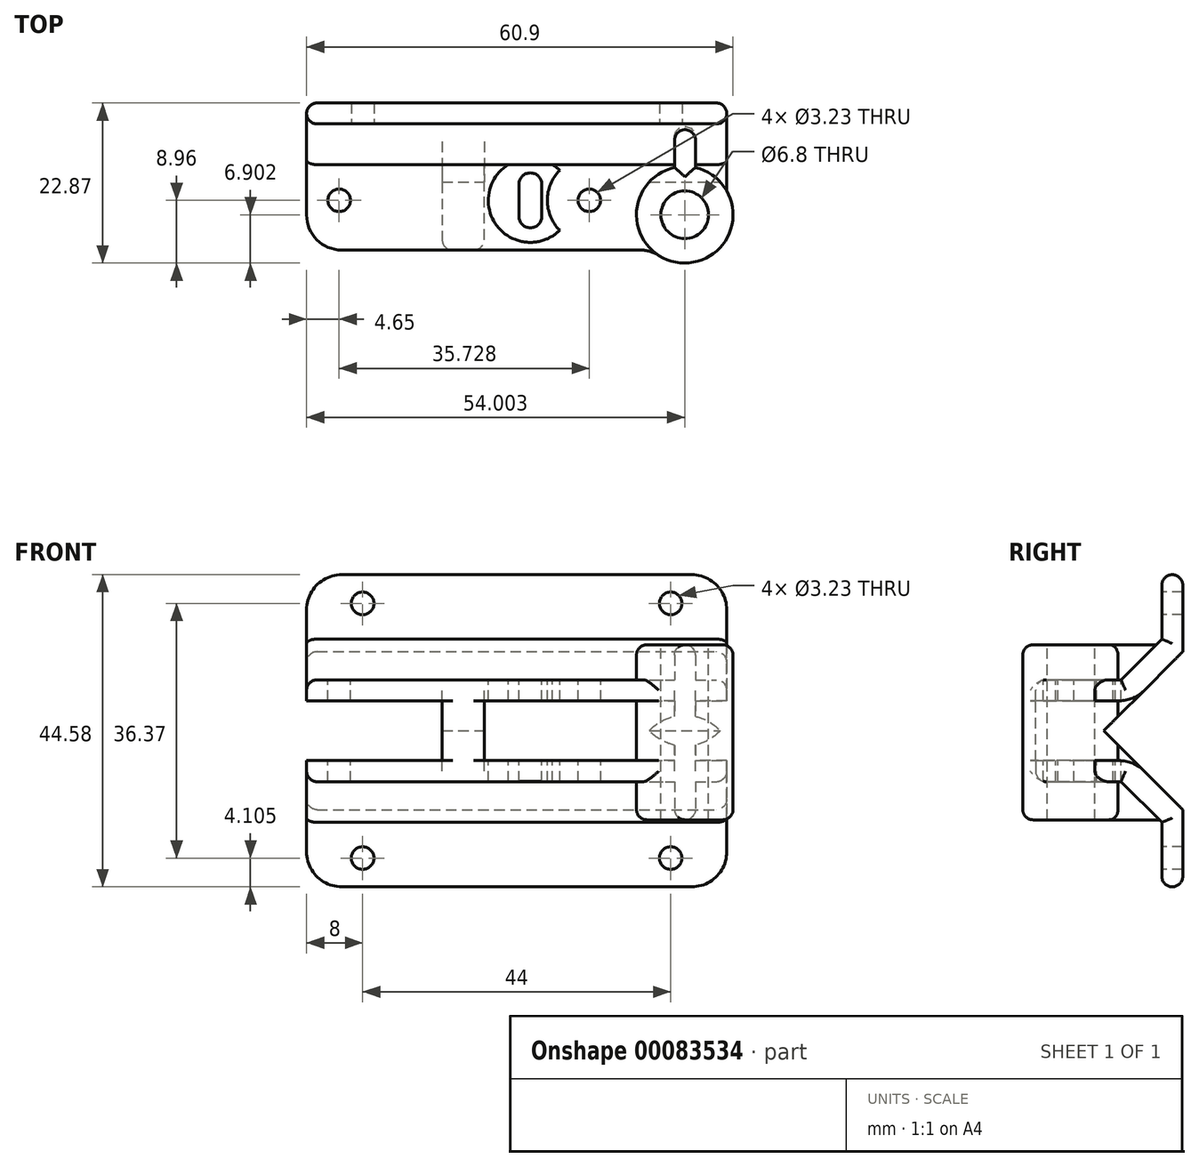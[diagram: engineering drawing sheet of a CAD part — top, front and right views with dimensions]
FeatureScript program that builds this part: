
annotation { "Feature Type Name" : "Feature", "Feature Type Description" : "" }
export const myFeature = defineFeature(function(context is Context, id is Id, definition is map)
    precondition{}
    {
        {
            var Q0;
            Q0=qCreatedBy(makeId("Right.planeOp"),FACE);
            var sketch = newSketch(context, id + "F0", { "sketchPlane" : qUnion([Q0])});
            skLineSegment(sketch, "E0", {"start": v(0, 0) * mm, "end": v(13.44, -13.44) * mm});
            skLineSegment(sketch, "E1", {"start": v(13.44, -13.44) * mm, "end": v(14.47, -12.4) * mm});
            skLineSegment(sketch, "E2", {"start": v(14.47, -12.4) * mm, "end": v(2.06, 0) * mm});
            skLineSegment(sketch, "E3", {"start": v(2.06, 0) * mm, "end": v(14.47, 12.4) * mm});
            skLineSegment(sketch, "E4", {"start": v(14.47, 12.4) * mm, "end": v(13.44, 13.44) * mm});
            skLineSegment(sketch, "E5", {"start": v(13.44, 13.44) * mm, "end": v(0, 0) * mm});
            skLineSegment(sketch, "E6", {"start": v(2.06, 0) * mm, "end": v(29.35, 0) * mm, "construction": true});
            skLineSegment(sketch, "E7.bottom", {"start": v(11.44, 23.19) * mm, "end": v(15.44, 23.19) * mm});
            skLineSegment(sketch, "E7.top", {"start": v(11.44, 13.19) * mm, "end": v(15.44, 13.19) * mm});
            skLineSegment(sketch, "E7.left", {"start": v(11.44, 23.19) * mm, "end": v(11.44, 13.19) * mm});
            skLineSegment(sketch, "E7.right", {"start": v(15.44, 23.19) * mm, "end": v(15.44, 13.19) * mm});
            skLineSegment(sketch, "E8", {"start": v(15.44, 18.19) * mm, "end": v(11.44, 18.19) * mm});
            skLineSegment(sketch, "E9", {"start": v(13.44, 23.19) * mm, "end": v(13.44, 13.19) * mm, "construction": true});
            skLineSegment(sketch, "E10", {"start": v(13.19, 23.19) * mm, "end": v(13.44, 22.94) * mm});
            skLineSegment(sketch, "E11", {"start": v(13.44, 22.94) * mm, "end": v(13.69, 23.19) * mm});
            skLineSegment(sketch, "E12", {"start": v(13.19, 13.19) * mm, "end": v(13.44, 13.44) * mm});
            skLineSegment(sketch, "E13", {"start": v(13.44, 13.44) * mm, "end": v(13.69, 13.19) * mm});
            skLineSegment(sketch, "E14.MirrorCS", {"start": v(12.4, 12.4) * mm, "end": v(13.44, 13.44) * mm});
            skLineSegment(sketch, "E15.MirrorCS", {"start": v(13.69, 23.19) * mm, "end": v(13.44, 22.94) * mm});
            skLineSegment(sketch, "E16.MirrorCS", {"start": v(13.44, 22.94) * mm, "end": v(13.19, 23.19) * mm});
            skLineSegment(sketch, "E17.MirrorCS", {"start": v(13.69, 13.19) * mm, "end": v(13.44, 13.44) * mm});
            skLineSegment(sketch, "E18.MirrorCS", {"start": v(15.44, 23.19) * mm, "end": v(11.44, 23.19) * mm});
            skLineSegment(sketch, "E19.MirrorCS", {"start": v(13.44, 13.44) * mm, "end": v(13.19, 13.19) * mm});
            skLineSegment(sketch, "E20.MirrorCS", {"start": v(11.44, 18.19) * mm, "end": v(15.44, 18.19) * mm});
            skLineSegment(sketch, "E21.MirrorCS", {"start": v(15.44, 13.19) * mm, "end": v(11.44, 13.19) * mm});
            skLineSegment(sketch, "E22", {"start": v(13.44, 13.44) * mm, "end": v(13.44, -13.44) * mm, "construction": true});
            skPoint(sketch, "E23", {"position": v(13.44, 0) * mm});
            skLineSegment(sketch, "E24", {"start": v(11.44, 19.74) * mm, "end": v(15.44, 19.74) * mm});
            skLineSegment(sketch, "E25.MirrorCS", {"start": v(11.44, 16.64) * mm, "end": v(15.44, 16.64) * mm});
            skLineSegment(sketch, "E26.MirrorCS", {"start": v(13.69, -13.19) * mm, "end": v(13.44, -13.44) * mm});
            skLineSegment(sketch, "E27.MirrorCS", {"start": v(13.19, -13.19) * mm, "end": v(13.44, -13.44) * mm});
            skLineSegment(sketch, "E28.MirrorCS", {"start": v(15.44, -13.19) * mm, "end": v(11.44, -13.19) * mm});
            skLineSegment(sketch, "E29.MirrorCS", {"start": v(13.44, -22.94) * mm, "end": v(13.19, -23.19) * mm});
            skLineSegment(sketch, "E30.MirrorCS", {"start": v(11.44, -23.19) * mm, "end": v(11.44, -13.19) * mm});
            skLineSegment(sketch, "E31.MirrorCS", {"start": v(15.44, -23.19) * mm, "end": v(11.44, -23.19) * mm});
            skLineSegment(sketch, "E32.MirrorCS", {"start": v(13.44, -22.94) * mm, "end": v(13.69, -23.19) * mm});
            skLineSegment(sketch, "E33.MirrorCS", {"start": v(14.47, -12.4) * mm, "end": v(13.44, -13.44) * mm});
            skLineSegment(sketch, "E34.MirrorCS", {"start": v(15.44, -23.19) * mm, "end": v(15.44, -13.19) * mm});
            skLineSegment(sketch, "E35.MirrorCS", {"start": v(15.44, -18.19) * mm, "end": v(11.44, -18.19) * mm});
            skLineSegment(sketch, "E36.MirrorCS", {"start": v(13.44, -13.44) * mm, "end": v(13.19, -13.19) * mm});
            skLineSegment(sketch, "E37.MirrorCS", {"start": v(11.44, -16.64) * mm, "end": v(15.44, -16.64) * mm});
            skLineSegment(sketch, "E38.MirrorCS", {"start": v(11.44, -19.74) * mm, "end": v(15.44, -19.74) * mm});
            skLineSegment(sketch, "E39.MirrorCS", {"start": v(13.19, -23.19) * mm, "end": v(13.44, -22.94) * mm});
            skLineSegment(sketch, "E40.MirrorCS", {"start": v(11.44, -23.19) * mm, "end": v(15.44, -23.19) * mm});
            skLineSegment(sketch, "E41.MirrorCS", {"start": v(11.44, -13.19) * mm, "end": v(15.44, -13.19) * mm});
            skLineSegment(sketch, "E42.MirrorCS", {"start": v(13.44, -23.19) * mm, "end": v(13.44, -13.19) * mm, "construction": true});
            skLineSegment(sketch, "E43.MirrorCS", {"start": v(13.44, -13.44) * mm, "end": v(13.69, -13.19) * mm});
            skLineSegment(sketch, "E44.MirrorCS", {"start": v(13.69, -23.19) * mm, "end": v(13.44, -22.94) * mm});
            skLineSegment(sketch, "E45.MirrorCS", {"start": v(11.44, -18.19) * mm, "end": v(15.44, -18.19) * mm});
            skLineSegment(sketch, "E46.MirrorCS", {"start": v(12.4, -12.4) * mm, "end": v(13.44, -13.44) * mm});
            skLineSegment(sketch, "E47", {"start": v(6.72, 6.72) * mm, "end": v(7.75, 5.69) * mm});
            skLineSegment(sketch, "E48.MirrorCS", {"start": v(15.44, 16.64) * mm, "end": v(11.44, 16.64) * mm});
            skLineSegment(sketch, "E49.MirrorCS", {"start": v(15.44, 19.74) * mm, "end": v(11.44, 19.74) * mm});
            skLineSegment(sketch, "E50.MirrorCS", {"start": v(-9.75, 2) * mm, "end": v(0.25, 2) * mm});
            skLineSegment(sketch, "E51.MirrorCS", {"start": v(0.25, 2) * mm, "end": v(0.25, -2) * mm});
            skLineSegment(sketch, "E52.MirrorCS", {"start": v(-9.75, -2) * mm, "end": v(0.25, -2) * mm});
            skLineSegment(sketch, "E53.MirrorCS", {"start": v(-9.75, 2) * mm, "end": v(-9.75, -2) * mm});
            skLineSegment(sketch, "E54.MirrorCS", {"start": v(-6.3, -2) * mm, "end": v(-6.3, 2) * mm});
            skLineSegment(sketch, "E55.MirrorCS", {"start": v(-4.75, -2) * mm, "end": v(-4.75, 2) * mm});
            skLineSegment(sketch, "E56.MirrorCS", {"start": v(-3.2, -2) * mm, "end": v(-3.2, 2) * mm});
            skLineSegment(sketch, "E57.MirrorCS", {"start": v(-9.75, 0.25) * mm, "end": v(-9.5, 0) * mm});
            skLineSegment(sketch, "E58.MirrorCS", {"start": v(-9.75, -0.25) * mm, "end": v(-9.5, 0) * mm});
            skLineSegment(sketch, "E59.MirrorCS", {"start": v(-9.75, 0) * mm, "end": v(0.25, 0) * mm, "construction": true});
            skLineSegment(sketch, "E60.bottom", {"start": v(-7.85, 4.27) * mm, "end": v(-1.65, 4.27) * mm});
            skLineSegment(sketch, "E60.top", {"start": v(-7.85, -4.28) * mm, "end": v(-1.65, -4.28) * mm});
            skLineSegment(sketch, "E60.left", {"start": v(-7.85, 4.27) * mm, "end": v(-7.85, -4.28) * mm});
            skLineSegment(sketch, "E60.right", {"start": v(-1.65, 4.27) * mm, "end": v(-1.65, -4.28) * mm});
            skPoint(sketch, "E61", {"position": v(-4.75, 0) * mm});
            skLineSegment(sketch, "E62", {"start": v(-7.85, -4.28) * mm, "end": v(-1.65, 4.27) * mm, "construction": true});
            skLineSegment(sketch, "E63", {"start": v(-7.85, 4.27) * mm, "end": v(-1.65, -4.28) * mm, "construction": true});
            skLineSegment(sketch, "E64.MirrorCS", {"start": v(9.16, 21.29) * mm, "end": v(9.16, 15.09) * mm});
            skLineSegment(sketch, "E65.MirrorCS", {"start": v(9.16, 15.09) * mm, "end": v(17.71, 15.09) * mm});
            skLineSegment(sketch, "E66.MirrorCS", {"start": v(9.16, 21.29) * mm, "end": v(17.71, 21.29) * mm});
            skLineSegment(sketch, "E67.MirrorCS", {"start": v(9.16, 21.29) * mm, "end": v(17.71, 15.09) * mm, "construction": true});
            skLineSegment(sketch, "E68.MirrorCS", {"start": v(17.71, 21.29) * mm, "end": v(9.16, 15.09) * mm, "construction": true});
            skLineSegment(sketch, "E69.MirrorCS", {"start": v(17.71, 21.29) * mm, "end": v(17.71, 15.09) * mm});
            skLineSegment(sketch, "E70.MirrorCS", {"start": v(9.16, -21.29) * mm, "end": v(9.16, -15.09) * mm});
            skLineSegment(sketch, "E71.MirrorCS", {"start": v(9.16, -21.29) * mm, "end": v(17.71, -15.09) * mm, "construction": true});
            skLineSegment(sketch, "E72.MirrorCS", {"start": v(17.71, -21.29) * mm, "end": v(9.16, -15.09) * mm, "construction": true});
            skLineSegment(sketch, "E73.MirrorCS", {"start": v(17.71, -21.29) * mm, "end": v(17.71, -15.09) * mm});
            skLineSegment(sketch, "E74.MirrorCS", {"start": v(9.16, -15.09) * mm, "end": v(17.71, -15.09) * mm});
            skLineSegment(sketch, "E75.MirrorCS", {"start": v(9.16, -21.29) * mm, "end": v(17.71, -21.29) * mm});
            skSolve(sketch);
        }
        {
            var Q0;
            Q0=qCreatedBy(makeId("Right.planeOp"),FACE);
            var sketch = newSketch(context, id + "F1", { "sketchPlane" : qUnion([Q0])});
            skLineSegment(sketch, "E76", {"start": v(9.16, 22.29) * mm, "end": v(9.16, 11.28) * mm});
            skLineSegment(sketch, "E77", {"start": v(9.16, 11.28) * mm, "end": v(2.15, 4.27) * mm});
            skLineSegment(sketch, "E78", {"start": v(2.15, 4.27) * mm, "end": v(-11.85, 4.27) * mm});
            skLineSegment(sketch, "E79", {"start": v(-11.85, 4.27) * mm, "end": v(-11.85, 7.27) * mm});
            skLineSegment(sketch, "E80", {"start": v(-11.85, 7.27) * mm, "end": v(0.35, 7.27) * mm});
            skLineSegment(sketch, "E81", {"start": v(0.35, 7.27) * mm, "end": v(6.16, 13.09) * mm});
            skLineSegment(sketch, "E82", {"start": v(6.16, 13.09) * mm, "end": v(6.16, 22.29) * mm});
            skLineSegment(sketch, "E83", {"start": v(6.16, 22.29) * mm, "end": v(9.16, 22.29) * mm});
            skLineSegment(sketch, "E84.MirrorCS", {"start": v(6.16, -13.09) * mm, "end": v(6.16, -22.29) * mm});
            skLineSegment(sketch, "E85.MirrorCS", {"start": v(9.16, -11.28) * mm, "end": v(2.15, -4.27) * mm});
            skLineSegment(sketch, "E86.MirrorCS", {"start": v(9.16, -22.29) * mm, "end": v(9.16, -11.28) * mm});
            skLineSegment(sketch, "E87.MirrorCS", {"start": v(-11.85, -4.27) * mm, "end": v(-11.85, -7.27) * mm});
            skLineSegment(sketch, "E88.MirrorCS", {"start": v(2.15, -4.27) * mm, "end": v(-11.85, -4.27) * mm});
            skLineSegment(sketch, "E89.MirrorCS", {"start": v(0.35, -7.27) * mm, "end": v(6.16, -13.09) * mm});
            skLineSegment(sketch, "E90.MirrorCS", {"start": v(-11.85, -7.27) * mm, "end": v(0.35, -7.27) * mm});
            skLineSegment(sketch, "E91.MirrorCS", {"start": v(6.16, -22.29) * mm, "end": v(9.16, -22.29) * mm});
            skLineSegment(sketch, "E92.0", {"start": v(13.44, 13.44) * mm, "end": v(0, 0) * mm});
            skSolve(sketch);
        }
        {
            var Q0;
            Q0=makeQuery(id+"F1.imprint","IMPRINT",FACE,{"disambiguationData":[TD([[makeQuery(id+"F1.imprint","IMPRINT",EDGE,{"derivedFrom":sQuery(id+"F1.wireOp",EDGE,"E76")}),-1.0]])]});
            var Q1;
            Q1=makeQuery(id+"F1.imprint","IMPRINT",FACE,{"disambiguationData":[TD([[makeQuery(id+"F1.imprint","IMPRINT",EDGE,{"derivedFrom":sQuery(id+"F1.wireOp",EDGE,"E84.MirrorCS")}),1.0]])]});
            extrude(context, id + "F2", {"entities" : qUnion([Q0, Q1]), "oppositeDirection" : true, "depth" : 60 * mm});
        }
        {
            var Q0;
            Q0=makeQuery(id+"F2.opExtrude","CAP_EDGE",EDGE,{"disambiguationData":[OSD([sQuery(id+"F1.wireOp",EDGE,"E79")])],"isStart":true});
            var Q1;
            Q1=makeQuery(id+"F2.opExtrude","CAP_EDGE",EDGE,{"disambiguationData":[OSD([sQuery(id+"F1.wireOp",EDGE,"E87.MirrorCS")])],"isStart":true});
            fillet(context, id + "F3", {"entities" : qUnion([Q0, Q1]), "radius" : 5 * mm, "tangentPropagation" : true, "allowEdgeOverflow" : false});
        }
        {
            var Q0;
            Q0=makeQuery(id+"F2.opExtrude","SWEPT_FACE",FACE,{"disambiguationData":[OSD([sQuery(id+"F1.wireOp",EDGE,"E82")])]});
            var sketch = newSketch(context, id + "F4", { "sketchPlane" : qUnion([Q0])});
            skLineSegment(sketch, "E93", {"start": v(0, 18.19) * mm, "end": v(-60, 18.19) * mm, "construction": true});
            skPoint(sketch, "E93.endSnap0", {"position": v(-60, 17.69) * mm});
            skPoint(sketch, "E94", {"position": v(-8, 18.19) * mm});
            skLineSegment(sketch, "E95", {"start": v(-30, 18.19) * mm, "end": v(-30, 14.6) * mm, "construction": true});
            skPoint(sketch, "E96.MirrorP", {"position": v(-52, 18.19) * mm});
            skLineSegment(sketch, "E97", {"start": v(0, 0) * mm, "end": v(-59.67, 0) * mm, "construction": true});
            skPoint(sketch, "E98.MirrorP", {"position": v(-52, -18.19) * mm});
            skPoint(sketch, "E99.MirrorP", {"position": v(-8, -18.19) * mm});
            skSolve(sketch);
        }
        {
            var Q0;
            Q0=sQuery(id+"F4.wireOp",VERTEX,"E94");
            var Q1;
            Q1=sQuery(id+"F4.wireOp",VERTEX,"E96.MirrorP");
            var Q2;
            Q2=sQuery(id+"F4.wireOp",VERTEX,"E98.MirrorP");
            var Q3;
            Q3=sQuery(id+"F4.wireOp",VERTEX,"E99.MirrorP");
            var Q4;
            Q4=makeQuery(id+"F2.opExtrude","SWEPT_BODY",BODY,{"disambiguationData":[OSD([sQuery(id+"F1.wireOp",EDGE,"E84.MirrorCS"),sQuery(id+"F1.wireOp",EDGE,"E85.MirrorCS"),sQuery(id+"F1.wireOp",EDGE,"E86.MirrorCS"),sQuery(id+"F1.wireOp",EDGE,"E87.MirrorCS"),sQuery(id+"F1.wireOp",EDGE,"E88.MirrorCS"),sQuery(id+"F1.wireOp",EDGE,"E89.MirrorCS"),sQuery(id+"F1.wireOp",EDGE,"E90.MirrorCS"),sQuery(id+"F1.wireOp",EDGE,"E91.MirrorCS")])]});
            var Q5;
            Q5=makeQuery(id+"F2.opExtrude","SWEPT_BODY",BODY,{"disambiguationData":[OSD([sQuery(id+"F1.wireOp",EDGE,"E76"),sQuery(id+"F1.wireOp",EDGE,"E77"),sQuery(id+"F1.wireOp",EDGE,"E78"),sQuery(id+"F1.wireOp",EDGE,"E79"),sQuery(id+"F1.wireOp",EDGE,"E80"),sQuery(id+"F1.wireOp",EDGE,"E81"),sQuery(id+"F1.wireOp",EDGE,"E82"),sQuery(id+"F1.wireOp",EDGE,"E83")])]});
            hole(context, id + "F5", {"style" : HoleStyle.SIMPLE, "endStyle" : HoleEndStyle.THROUGH, "holeDiameter" : 3.23 * mm, "locations" : qUnion([Q0, Q1, Q2, Q3]), "scope" : qUnion([Q4, Q5]), "isTappedThrough" : true});
        }
        {
            var Q0;
            Q0=makeQuery(id+"F2.opExtrude","SWEPT_FACE",FACE,{"disambiguationData":[OSD([sQuery(id+"F1.wireOp",EDGE,"E80")])]});
            var sketch = newSketch(context, id + "F6", { "sketchPlane" : qUnion([Q0])});
            skCircle(sketch, "E100", {"center": v(-6, -6.8) * mm, "radius": 3.4 * mm});
            skCircle(sketch, "E101", {"center": v(-6, -6.8) * mm, "radius": 6.9 * mm});
            skLineSegment(sketch, "E102", {"start": v(-60, -4.75) * mm, "end": v(0, -4.75) * mm, "construction": true});
            skCircle(sketch, "E103", {"center": v(-55.35, -4.75) * mm, "radius": 6 * mm});
            skCircle(sketch, "E104", {"center": v(-19.62, -4.75) * mm, "radius": 6 * mm});
            skLineSegment(sketch, "E105.bottom", {"start": v(-40.64, -11.85) * mm, "end": v(-34.64, -11.85) * mm});
            skLineSegment(sketch, "E105.top", {"start": v(-40.64, 2.15) * mm, "end": v(-34.64, 2.15) * mm});
            skLineSegment(sketch, "E105.left", {"start": v(-40.64, -11.85) * mm, "end": v(-40.64, 2.15) * mm});
            skLineSegment(sketch, "E105.right", {"start": v(-34.64, -11.85) * mm, "end": v(-34.64, 2.15) * mm});
            skLineSegment(sketch, "E106.bottom", {"start": v(-23.35, -11.85) * mm, "end": v(-29.35, -11.85) * mm});
            skCircle(sketch, "E107", {"center": v(-55.35, -4.75) * mm, "radius": 1.65 * mm});
            skCircle(sketch, "E108", {"center": v(-48.02, -4.75) * mm, "radius": 6 * mm});
            skCircle(sketch, "E109", {"center": v(-28.05, -4.75) * mm, "radius": 6 * mm});
            skLineSegment(sketch, "E110", {"start": v(-28.05, -2.46) * mm, "end": v(-28.05, -7.7) * mm, "construction": true});
            skArc(sketch, "E111", {"start": v(-29.68, -2.46) * mm, "mid": v(-28.05, -0.83) * mm, "end": v(-26.41, -2.46) * mm});
            skArc(sketch, "E112.MirrorCS", {"start": v(-29.68, -7.04) * mm, "mid": v(-28.05, -8.67) * mm, "end": v(-26.41, -7.04) * mm});
            skLineSegment(sketch, "E113", {"start": v(-26.41, -7.04) * mm, "end": v(-26.41, -2.46) * mm});
            skLineSegment(sketch, "E114", {"start": v(-29.68, -7.04) * mm, "end": v(-29.68, -2.46) * mm});
            skLineSegment(sketch, "E115.bottom", {"start": v(-7.46, 6.16) * mm, "end": v(-4.46, 6.16) * mm});
            skLineSegment(sketch, "E115.left", {"start": v(-7.46, 6.16) * mm, "end": v(-7.46, -0.07) * mm});
            skLineSegment(sketch, "E115.right", {"start": v(-4.46, 6.16) * mm, "end": v(-4.46, -0.08) * mm});
            skSolve(sketch);
        }
        {
            var Q0;
            {var subQ0=sQuery(id+"F6.wireOp",EDGE,"E101");var subQ1=makeQuery(id+"F2.opExtrude","SWEPT_EDGE",EDGE,{"disambiguationData":[OSD([sQuery(id+"F1.wireOp",EDGE,"E79"),sQuery(id+"F1.wireOp",EDGE,"E80")])]});var subQ2=makeQuery(id+"F6.imprint","INTERSECT",VERTEX,{"disambiguationData":[OD(0.0)],"derivedFrom":[subQ1,subQ0]});Q0=makeQuery(id+"F6.imprint","IMPRINT",FACE,{"disambiguationData":[TD([[makeQuery(id+"F6.imprint","IMPRINT",EDGE,{"disambiguationData":[TD([[subQ2,-1.0]])],"derivedFrom":subQ0}),1.0]])]});}
            var Q1;
            Q1=makeQuery(id+"F6.imprint","IMPRINT",FACE,{"disambiguationData":[TD([[makeQuery(id+"F6.imprint","IMPRINT",EDGE,{"derivedFrom":sQuery(id+"F6.wireOp",EDGE,"E100")}),1.0]])]});
            var Q2;
            {var subQ1=sQuery(id+"F6.wireOp",EDGE,"E115.bottom");Q2=makeQuery(id+"F6.imprint","IMPRINT",FACE,{"disambiguationData":[TD([[makeQuery(id+"F6.imprint","IMPRINT",EDGE,{"derivedFrom":subQ1}),-1.0]])]});}
            var Q3;
            {var subQ0=sQuery(id+"F6.wireOp",EDGE,"E115.right");var subQ1=sQuery(id+"F6.wireOp",EDGE,"E101");var subQ2=makeQuery(id+"F6.imprint","INTERSECT",VERTEX,{"derivedFrom":[subQ1,subQ0]});Q3=makeQuery(id+"F6.imprint","IMPRINT",FACE,{"disambiguationData":[TD([[makeQuery(id+"F6.imprint","IMPRINT",EDGE,{"disambiguationData":[TD([[subQ2,-1.0]])],"derivedFrom":subQ1}),-1.0]])]});}
            var Q4;
            {var subQ0=sQuery(id+"F6.wireOp",EDGE,"E115.left");var subQ1=sQuery(id+"F6.wireOp",EDGE,"E101");var subQ2=makeQuery(id+"F6.imprint","INTERSECT",VERTEX,{"derivedFrom":[subQ1,subQ0]});Q4=makeQuery(id+"F6.imprint","IMPRINT",FACE,{"disambiguationData":[TD([[makeQuery(id+"F6.imprint","IMPRINT",EDGE,{"disambiguationData":[TD([[subQ2,1.0]])],"derivedFrom":subQ1}),-1.0]])]});}
            var Q5;
            Q5=makeQuery(id+"F6.imprint","IMPRINT",FACE,{"disambiguationData":[TD([[makeQuery(id+"F6.imprint","IMPRINT",EDGE,{"derivedFrom":sQuery(id+"F6.wireOp",EDGE,"E100")}),-1.0]])]});
            extrude(context, id + "F7", {"entities" : qUnion([Q0, Q1, Q2, Q3, Q4, Q5]), "operationType" : NewBodyOperationType.ADD, "depth" : 5 * mm, "hasSecondDirection" : true, "secondDirectionOppositeDirection" : true, "secondDirectionDepth" : 20 * mm});
        }
        {
            var Q0;
            Q0=makeQuery(id+"F6.imprint","IMPRINT",FACE,{"disambiguationData":[TD([[makeQuery(id+"F6.imprint","IMPRINT",EDGE,{"derivedFrom":sQuery(id+"F6.wireOp",EDGE,"E100")}),1.0]])]});
            extrude(context, id + "F8", {"entities" : qUnion([Q0]), "operationType" : NewBodyOperationType.REMOVE, "endBound" : BoundingType.THROUGH_ALL, "oppositeDirection" : true, "depth" : 25 * mm, "hasSecondDirection" : true, "secondDirectionBound" : SecondDirectionBoundingType.THROUGH_ALL, "secondDirectionOppositeDirection" : false, "secondDirectionDepth" : 25 * mm});
        }
        {
            var Q0;
            Q0=sQuery(id+"F6.wireOp",VERTEX,"E103.center");
            var Q1;
            Q1=sQuery(id+"F6.wireOp",VERTEX,"E104.center");
            var Q2;
            Q2=makeQuery(id+"F2.opExtrude","SWEPT_BODY",BODY,{"disambiguationData":[OSD([sQuery(id+"F1.wireOp",EDGE,"E76"),sQuery(id+"F1.wireOp",EDGE,"E77"),sQuery(id+"F1.wireOp",EDGE,"E78"),sQuery(id+"F1.wireOp",EDGE,"E79"),sQuery(id+"F1.wireOp",EDGE,"E80"),sQuery(id+"F1.wireOp",EDGE,"E81"),sQuery(id+"F1.wireOp",EDGE,"E82"),sQuery(id+"F1.wireOp",EDGE,"E83")])]});
            hole(context, id + "F9", {"style" : HoleStyle.SIMPLE, "endStyle" : HoleEndStyle.THROUGH, "holeDiameter" : 3.23 * mm, "locations" : qUnion([Q0, Q1]), "scope" : qUnion([Q2]), "isTappedThrough" : true});
        }
        {
            var Q0;
            {var subQ0=sQuery(id+"F1.wireOp",EDGE,"E80");Q0=makeQuery(id+"F7.boolean.opBoolean","MERGE",FACE,{"derivedFrom":[makeQuery(id+"F2.opExtrude","CAP_FACE",FACE,{"disambiguationData":[OSD([sQuery(id+"F1.wireOp",EDGE,"E76"),sQuery(id+"F1.wireOp",EDGE,"E77"),sQuery(id+"F1.wireOp",EDGE,"E78"),sQuery(id+"F1.wireOp",EDGE,"E79"),subQ0,sQuery(id+"F1.wireOp",EDGE,"E81"),sQuery(id+"F1.wireOp",EDGE,"E82"),sQuery(id+"F1.wireOp",EDGE,"E83")])],"isStart":true}),makeQuery(id+"F2.opExtrude","CAP_FACE",FACE,{"disambiguationData":[OSD([sQuery(id+"F1.wireOp",EDGE,"E84.MirrorCS"),sQuery(id+"F1.wireOp",EDGE,"E85.MirrorCS"),sQuery(id+"F1.wireOp",EDGE,"E86.MirrorCS"),sQuery(id+"F1.wireOp",EDGE,"E87.MirrorCS"),sQuery(id+"F1.wireOp",EDGE,"E88.MirrorCS"),sQuery(id+"F1.wireOp",EDGE,"E89.MirrorCS"),sQuery(id+"F1.wireOp",EDGE,"E90.MirrorCS"),sQuery(id+"F1.wireOp",EDGE,"E91.MirrorCS")])],"isStart":true}),makeQuery(id+"F7.opExtrude","SWEPT_FACE",FACE,{"disambiguationData":[OSD([subQ0])]})]});}
            var sketch = newSketch(context, id + "F10", { "sketchPlane" : qUnion([Q0])});
            skLineSegment(sketch, "E116", {"start": v(2.15, -4.27) * mm, "end": v(-2.12, 0) * mm});
            skLineSegment(sketch, "E117", {"start": v(-2.12, 0) * mm, "end": v(2.15, 4.27) * mm});
            skLineSegment(sketch, "E118", {"start": v(2.15, 4.27) * mm, "end": v(9.16, 11.28) * mm});
            skLineSegment(sketch, "E119", {"start": v(9.16, 11.28) * mm, "end": v(9.16, -11.28) * mm});
            skLineSegment(sketch, "E120", {"start": v(9.16, -11.28) * mm, "end": v(2.15, -4.27) * mm});
            skSolve(sketch);
        }
        {
            var Q0;
            Q0=makeQuery(id+"F6.imprint","IMPRINT",FACE,{"disambiguationData":[TD([[makeQuery(id+"F6.imprint","IMPRINT",EDGE,{"derivedFrom":sQuery(id+"F6.wireOp",EDGE,"E111")}),-1.0]])]});
            extrude(context, id + "F11", {"entities" : qUnion([Q0]), "operationType" : NewBodyOperationType.REMOVE, "endBound" : BoundingType.THROUGH_ALL, "oppositeDirection" : true, "depth" : 25 * mm});
        }
        {
            var Q0;
            {var subQ0=sQuery(id+"F6.wireOp",EDGE,"E105.bottom");Q0=makeQuery(id+"F6.imprint","IMPRINT",FACE,{"disambiguationData":[TD([[makeQuery(id+"F6.imprint","IMPRINT",EDGE,{"derivedFrom":subQ0}),1.0]])]});}
            var Q1;
            {var subQ0=sQuery(id+"F6.wireOp",EDGE,"E105.top");Q1=makeQuery(id+"F6.imprint","IMPRINT",FACE,{"disambiguationData":[TD([[makeQuery(id+"F6.imprint","IMPRINT",EDGE,{"derivedFrom":subQ0}),-1.0]])]});}
            var Q2;
            {var subQ0=sQuery(id+"F1.wireOp",EDGE,"E85.MirrorCS");var subQ1=sQuery(id+"F1.wireOp",EDGE,"E91.MirrorCS");var subQ2=sQuery(id+"F1.wireOp",EDGE,"E90.MirrorCS");var subQ3=sQuery(id+"F1.wireOp",EDGE,"E89.MirrorCS");var subQ4=sQuery(id+"F1.wireOp",EDGE,"E88.MirrorCS");var subQ5=sQuery(id+"F1.wireOp",EDGE,"E87.MirrorCS");var subQ6=sQuery(id+"F1.wireOp",EDGE,"E86.MirrorCS");var subQ7=sQuery(id+"F1.wireOp",EDGE,"E84.MirrorCS");var subQ8=sQuery(id+"F1.wireOp",EDGE,"E80");Q2=makeQuery(id+"F7.boolean.opBoolean","SPLIT",FACE,{"disambiguationData":[TD([makeQuery(id+"F2.opExtrude","CAP_FACE",FACE,{"disambiguationData":[OSD([sQuery(id+"F1.wireOp",EDGE,"E76"),sQuery(id+"F1.wireOp",EDGE,"E77"),sQuery(id+"F1.wireOp",EDGE,"E78"),sQuery(id+"F1.wireOp",EDGE,"E79"),subQ8,sQuery(id+"F1.wireOp",EDGE,"E81"),sQuery(id+"F1.wireOp",EDGE,"E82"),sQuery(id+"F1.wireOp",EDGE,"E83")])],"isStart":true}),makeQuery(id+"F2.opExtrude","CAP_FACE",FACE,{"disambiguationData":[OSD([subQ7,subQ0,subQ6,subQ5,subQ4,subQ3,subQ2,subQ1])],"isStart":true}),makeQuery(id+"F2.opExtrude","CAP_FACE",FACE,{"disambiguationData":[OSD([subQ7,subQ0,subQ6,subQ5,subQ4,subQ3,subQ2,subQ1])],"isStart":false}),makeQuery(id+"F2.opExtrude","SWEPT_FACE",FACE,{"disambiguationData":[OSD([subQ0])]}),makeQuery(id+"F2.opExtrude","SWEPT_FACE",FACE,{"disambiguationData":[OSD([subQ5])]}),makeQuery(id+"F7.opExtrude","SWEPT_FACE",FACE,{"disambiguationData":[OSD([sQuery(id+"F6.wireOp",EDGE,"E101")])]}),makeQuery(id+"F7.opExtrude","SWEPT_FACE",FACE,{"disambiguationData":[OSD([subQ8])]})])],"derivedFrom":makeQuery(id+"F2.opExtrude","SWEPT_FACE",FACE,{"disambiguationData":[OSD([subQ4])]})});}
            extrude(context, id + "F12", {"entities" : qUnion([Q0, Q1]), "operationType" : NewBodyOperationType.ADD, "endBound" : BoundingType.UP_TO_SURFACE, "oppositeDirection" : true, "endBoundEntityFace" : qUnion([Q2]), "depth" : 25 * mm});
        }
        {
            var Q0;
            {var subQ0=sQuery(id+"F10.wireOp",EDGE,"xsKBfpLQ-1iq2-Bcec-7IUX-g84XxdSZJY2x");Q0=makeQuery(id+"F10.imprint","IMPRINT",FACE,{"disambiguationData":[TD([[makeQuery(id+"F10.imprint","IMPRINT",EDGE,{"derivedFrom":subQ0}),-1.0]])]});}
            var Q1;
            {var subQ0=sQuery(id+"F10.wireOp",EDGE,"E117");var subQ1=sQuery(id+"F10.wireOp",EDGE,"E116");var subQ2=makeQuery(id+"F10.imprint","INTERSECT",VERTEX,{"derivedFrom":[subQ1,subQ0]});Q1=makeQuery(id+"F10.imprint","IMPRINT",FACE,{"disambiguationData":[TD([[makeQuery(id+"F10.imprint","IMPRINT",EDGE,{"disambiguationData":[TD([[subQ2,1.0]])],"derivedFrom":subQ1}),-1.0]])]});}
            extrude(context, id + "F13", {"entities" : qUnion([Q0, Q1]), "operationType" : NewBodyOperationType.REMOVE, "endBound" : BoundingType.THROUGH_ALL, "oppositeDirection" : true, "depth" : 25 * mm});
        }
        {
            var Q0;
            Q0=makeQuery(id+"F2.opExtrude","CAP_EDGE",EDGE,{"disambiguationData":[OSD([sQuery(id+"F1.wireOp",EDGE,"E83")])],"isStart":true});
            var Q1;
            Q1=makeQuery(id+"F2.opExtrude","CAP_EDGE",EDGE,{"disambiguationData":[OSD([sQuery(id+"F1.wireOp",EDGE,"E83")])],"isStart":false});
            var Q2;
            Q2=makeQuery(id+"F2.opExtrude","CAP_EDGE",EDGE,{"disambiguationData":[OSD([sQuery(id+"F1.wireOp",EDGE,"E91.MirrorCS")])],"isStart":true});
            var Q3;
            Q3=makeQuery(id+"F2.opExtrude","CAP_EDGE",EDGE,{"disambiguationData":[OSD([sQuery(id+"F1.wireOp",EDGE,"E91.MirrorCS")])],"isStart":false});
            var Q4;
            Q4=makeQuery(id+"F2.opExtrude","CAP_EDGE",EDGE,{"disambiguationData":[OSD([sQuery(id+"F1.wireOp",EDGE,"E87.MirrorCS")])],"isStart":false});
            var Q5;
            Q5=makeQuery(id+"F2.opExtrude","CAP_EDGE",EDGE,{"disambiguationData":[OSD([sQuery(id+"F1.wireOp",EDGE,"E79")])],"isStart":false});
            var Q6;
            Q6=makeQuery(id+"F7.boolean.opBoolean","INTERSECT",EDGE,{"derivedFrom":[makeQuery(id+"F2.opExtrude","SWEPT_FACE",FACE,{"disambiguationData":[OSD([sQuery(id+"F1.wireOp",EDGE,"E87.MirrorCS")])]}),makeQuery(id+"F7.opExtrude","SWEPT_FACE",FACE,{"disambiguationData":[OSD([sQuery(id+"F6.wireOp",EDGE,"E101")])]})]});
            var Q7;
            Q7=makeQuery(id+"F7.boolean.opBoolean","INTERSECT",EDGE,{"derivedFrom":[makeQuery(id+"F2.opExtrude","SWEPT_FACE",FACE,{"disambiguationData":[OSD([sQuery(id+"F1.wireOp",EDGE,"E79")])]}),makeQuery(id+"F7.opExtrude","SWEPT_FACE",FACE,{"disambiguationData":[OSD([sQuery(id+"F6.wireOp",EDGE,"E101")])]})]});
            fillet(context, id + "F14", {"entities" : qUnion([Q0, Q1, Q2, Q3, Q4, Q5, Q6, Q7]), "radius" : 5 * mm, "tangentPropagation" : true, "allowEdgeOverflow" : false});
        }
        {
            var Q0;
            Q0=makeQuery(id+"F7.opExtrude","CAP_EDGE",EDGE,{"disambiguationData":[OSD([sQuery(id+"F6.wireOp",EDGE,"E101")])],"isStart":false});
            var Q1;
            Q1=makeQuery(id+"F2.opExtrude","SWEPT_EDGE",EDGE,{"disambiguationData":[OSD([sQuery(id+"F1.wireOp",EDGE,"E79"),sQuery(id+"F1.wireOp",EDGE,"E80")])]});
            var Q2;
            Q2=makeQuery(id+"F2.opExtrude","SWEPT_EDGE",EDGE,{"disambiguationData":[OSD([sQuery(id+"F1.wireOp",EDGE,"E82"),sQuery(id+"F1.wireOp",EDGE,"E83")])]});
            var Q3;
            Q3=makeQuery(id+"F2.opExtrude","CAP_EDGE",EDGE,{"disambiguationData":[OSD([sQuery(id+"F1.wireOp",EDGE,"E81")])],"isStart":false});
            var Q4;
            Q4=makeQuery(id+"F2.opExtrude","CAP_EDGE",EDGE,{"disambiguationData":[OSD([sQuery(id+"F1.wireOp",EDGE,"E81")])],"isStart":true});
            var Q5;
            Q5=makeQuery(id+"F2.opExtrude","CAP_EDGE",EDGE,{"disambiguationData":[OSD([sQuery(id+"F1.wireOp",EDGE,"E80")])],"isStart":true});
            var Q6;
            Q6=makeQuery(id+"F7.opExtrude","CAP_EDGE",EDGE,{"disambiguationData":[OSD([sQuery(id+"F6.wireOp",EDGE,"E115.right")])],"isStart":false});
            var Q7;
            Q7=makeQuery(id+"F7.opExtrude","CAP_EDGE",EDGE,{"disambiguationData":[OSD([sQuery(id+"F6.wireOp",EDGE,"E115.left")])],"isStart":false});
            var Q8;
            Q8=makeQuery(id+"F2.opExtrude","SWEPT_EDGE",EDGE,{"disambiguationData":[OSD([sQuery(id+"F1.wireOp",EDGE,"E76"),sQuery(id+"F1.wireOp",EDGE,"E83")])]});
            var Q9;
            Q9=makeQuery(id+"F12.opExtrude","SWEPT_EDGE",EDGE,{"disambiguationData":[OSD([sQuery(id+"F1.wireOp",EDGE,"E79"),sQuery(id+"F1.wireOp",EDGE,"E80"),sQuery(id+"F6.wireOp",EDGE,"E105.bottom"),sQuery(id+"F6.wireOp",EDGE,"E105.left")])]});
            var Q10;
            Q10=makeQuery(id+"F12.opExtrude","SWEPT_EDGE",EDGE,{"disambiguationData":[OSD([sQuery(id+"F1.wireOp",EDGE,"E79"),sQuery(id+"F1.wireOp",EDGE,"E80"),sQuery(id+"F6.wireOp",EDGE,"E105.bottom"),sQuery(id+"F6.wireOp",EDGE,"E105.right")])]});
            var Q11;
            Q11=makeQuery(id+"F2.opExtrude","SWEPT_EDGE",EDGE,{"disambiguationData":[OSD([sQuery(id+"F1.wireOp",EDGE,"E87.MirrorCS"),sQuery(id+"F1.wireOp",EDGE,"E90.MirrorCS")])]});
            var Q12;
            Q12=makeQuery(id+"F2.opExtrude","CAP_EDGE",EDGE,{"disambiguationData":[OSD([sQuery(id+"F1.wireOp",EDGE,"E89.MirrorCS")])],"isStart":false});
            var Q13;
            Q13=makeQuery(id+"F14.opFillet","BLEND_EDGE",EDGE,{"blendedFrom":[makeQuery(id+"F2.opExtrude","CAP_EDGE",EDGE,{"disambiguationData":[OSD([sQuery(id+"F1.wireOp",EDGE,"E91.MirrorCS")])],"isStart":false}),makeQuery(id+"F2.opExtrude","SWEPT_FACE",FACE,{"disambiguationData":[OSD([sQuery(id+"F1.wireOp",EDGE,"E84.MirrorCS")])]})],"blendedInto":[makeQuery(id+"F2.opExtrude","SWEPT_FACE",FACE,{"disambiguationData":[OSD([sQuery(id+"F1.wireOp",EDGE,"E84.MirrorCS")])]})]});
            var Q14;
            Q14=makeQuery(id+"F2.opExtrude","CAP_EDGE",EDGE,{"disambiguationData":[OSD([sQuery(id+"F1.wireOp",EDGE,"E89.MirrorCS")])],"isStart":true});
            var Q15;
            Q15=makeQuery(id+"F2.opExtrude","CAP_EDGE",EDGE,{"disambiguationData":[OSD([sQuery(id+"F1.wireOp",EDGE,"E90.MirrorCS")])],"isStart":true});
            var Q16;
            Q16=makeQuery(id+"F7.opExtrude","CAP_EDGE",EDGE,{"disambiguationData":[OSD([sQuery(id+"F6.wireOp",EDGE,"E115.right")])],"isStart":true});
            var Q17;
            Q17=makeQuery(id+"F7.opExtrude","CAP_EDGE",EDGE,{"disambiguationData":[OSD([sQuery(id+"F6.wireOp",EDGE,"E115.left")])],"isStart":true});
            var Q18;
            Q18=makeQuery(id+"F7.opExtrude","CAP_EDGE",EDGE,{"disambiguationData":[OSD([sQuery(id+"F6.wireOp",EDGE,"E101")])],"isStart":true});
            var Q19;
            Q19=makeQuery(id+"F2.opExtrude","SWEPT_EDGE",EDGE,{"disambiguationData":[OSD([sQuery(id+"F1.wireOp",EDGE,"E86.MirrorCS"),sQuery(id+"F1.wireOp",EDGE,"E91.MirrorCS")])]});
            fillet(context, id + "F15", {"entities" : qUnion([Q0, Q1, Q2, Q3, Q4, Q5, Q6, Q7, Q8, Q9, Q10, Q11, Q12, Q13, Q14, Q15, Q16, Q17, Q18, Q19]), "radius" : 1.5 * mm, "tangentPropagation" : true, "allowEdgeOverflow" : false});
        }
        {
            var Q0;
            {var subQ0=makeQuery(id+"F7.opExtrude","SWEPT_FACE",FACE,{"disambiguationData":[OSD([sQuery(id+"F6.wireOp",EDGE,"E115.left")])]});var subQ1=sQuery(id+"F1.wireOp",EDGE,"E85.MirrorCS");var subQ3=sQuery(id+"F1.wireOp",EDGE,"E88.MirrorCS");Q0=makeQuery(id+"F12.boolean.opBoolean","SPLIT",EDGE,{"disambiguationData":[TD([subQ0])],"derivedFrom":makeQuery(id+"F7.boolean.opBoolean","SPLIT",EDGE,{"disambiguationData":[TD([subQ0])],"derivedFrom":makeQuery(id+"F2.opExtrude","SWEPT_EDGE",EDGE,{"disambiguationData":[OSD([subQ1,subQ3])]})})});}
            var Q1;
            {var subQ0=sQuery(id+"F1.wireOp",EDGE,"E88.MirrorCS");var subQ2=sQuery(id+"F1.wireOp",EDGE,"E85.MirrorCS");Q1=makeQuery(id+"F12.boolean.opBoolean","SPLIT",EDGE,{"disambiguationData":[TD([makeQuery(id+"F12.opExtrude","SWEPT_FACE",FACE,{"disambiguationData":[OSD([sQuery(id+"F6.wireOp",EDGE,"E105.left")])]})])],"derivedFrom":makeQuery(id+"F7.boolean.opBoolean","SPLIT",EDGE,{"disambiguationData":[TD([makeQuery(id+"F7.opExtrude","SWEPT_FACE",FACE,{"disambiguationData":[OSD([sQuery(id+"F6.wireOp",EDGE,"E115.left")])]})])],"derivedFrom":makeQuery(id+"F2.opExtrude","SWEPT_EDGE",EDGE,{"disambiguationData":[OSD([subQ2,subQ0])]})})});}
            var Q2;
            {var subQ0=sQuery(id+"F1.wireOp",EDGE,"E78");var subQ1=makeQuery(id+"F2.opExtrude","SWEPT_FACE",FACE,{"disambiguationData":[OSD([subQ0])]});var subQ2=sQuery(id+"F1.wireOp",EDGE,"E77");var subQ3=makeQuery(id+"F2.opExtrude","SWEPT_FACE",FACE,{"disambiguationData":[OSD([subQ2])]});var subQ4=makeQuery(id+"F2.opExtrude","CAP_FACE",FACE,{"disambiguationData":[OSD([sQuery(id+"F1.wireOp",EDGE,"E76"),subQ2,subQ0,sQuery(id+"F1.wireOp",EDGE,"E79"),sQuery(id+"F1.wireOp",EDGE,"E80"),sQuery(id+"F1.wireOp",EDGE,"E81"),sQuery(id+"F1.wireOp",EDGE,"E82"),sQuery(id+"F1.wireOp",EDGE,"E83")])],"isStart":false});Q2=makeQuery(id+"F12.boolean.opBoolean","SPLIT",EDGE,{"disambiguationData":[TD([subQ4,subQ3,subQ1,makeQuery(id+"F12.opExtrude","SWEPT_FACE",FACE,{"disambiguationData":[OSD([sQuery(id+"F6.wireOp",EDGE,"E105.top")])]}),makeQuery(id+"F12.opExtrude","SWEPT_FACE",FACE,{"disambiguationData":[OSD([sQuery(id+"F6.wireOp",EDGE,"E105.left")])]})])],"derivedFrom":makeQuery(id+"F7.boolean.opBoolean","SPLIT",EDGE,{"disambiguationData":[TD([makeQuery(id+"F7.opExtrude","SWEPT_FACE",FACE,{"disambiguationData":[OSD([sQuery(id+"F6.wireOp",EDGE,"E115.left")])]})])],"derivedFrom":makeQuery(id+"F2.opExtrude","SWEPT_EDGE",EDGE,{"disambiguationData":[OSD([subQ2,subQ0])]})})});}
            var Q3;
            {var subQ0=makeQuery(id+"F7.opExtrude","SWEPT_FACE",FACE,{"disambiguationData":[OSD([sQuery(id+"F6.wireOp",EDGE,"E115.left")])]});var subQ1=sQuery(id+"F1.wireOp",EDGE,"E78");var subQ2=makeQuery(id+"F2.opExtrude","SWEPT_FACE",FACE,{"disambiguationData":[OSD([subQ1])]});var subQ3=sQuery(id+"F1.wireOp",EDGE,"E77");var subQ4=makeQuery(id+"F2.opExtrude","SWEPT_FACE",FACE,{"disambiguationData":[OSD([subQ3])]});Q3=makeQuery(id+"F12.boolean.opBoolean","SPLIT",EDGE,{"disambiguationData":[TD([subQ4,subQ2,subQ0,makeQuery(id+"F12.opExtrude","SWEPT_FACE",FACE,{"disambiguationData":[OSD([sQuery(id+"F6.wireOp",EDGE,"E105.top")])]}),makeQuery(id+"F12.opExtrude","SWEPT_FACE",FACE,{"disambiguationData":[OSD([sQuery(id+"F6.wireOp",EDGE,"E105.right")])]})])],"derivedFrom":makeQuery(id+"F7.boolean.opBoolean","SPLIT",EDGE,{"disambiguationData":[TD([subQ0])],"derivedFrom":makeQuery(id+"F2.opExtrude","SWEPT_EDGE",EDGE,{"disambiguationData":[OSD([subQ3,subQ1])]})})});}
            var Q4;
            {var subQ0=sQuery(id+"F1.wireOp",EDGE,"E78");var subQ1=sQuery(id+"F1.wireOp",EDGE,"E77");Q4=makeQuery(id+"F7.boolean.opBoolean","SPLIT",EDGE,{"disambiguationData":[TD([makeQuery(id+"F7.opExtrude","SWEPT_FACE",FACE,{"disambiguationData":[OSD([sQuery(id+"F6.wireOp",EDGE,"E115.right")])]})])],"derivedFrom":makeQuery(id+"F2.opExtrude","SWEPT_EDGE",EDGE,{"disambiguationData":[OSD([subQ1,subQ0])]})});}
            var Q5;
            {var subQ0=sQuery(id+"F1.wireOp",EDGE,"E88.MirrorCS");var subQ1=sQuery(id+"F1.wireOp",EDGE,"E85.MirrorCS");Q5=makeQuery(id+"F7.boolean.opBoolean","SPLIT",EDGE,{"disambiguationData":[TD([makeQuery(id+"F7.opExtrude","SWEPT_FACE",FACE,{"disambiguationData":[OSD([sQuery(id+"F6.wireOp",EDGE,"E115.right")])]})])],"derivedFrom":makeQuery(id+"F2.opExtrude","SWEPT_EDGE",EDGE,{"disambiguationData":[OSD([subQ1,subQ0])]})});}
            fillet(context, id + "F16", {"entities" : qUnion([Q0, Q1, Q2, Q3, Q4, Q5]), "radius" : 5 * mm, "tangentPropagation" : true, "allowEdgeOverflow" : false});
        }
    });
